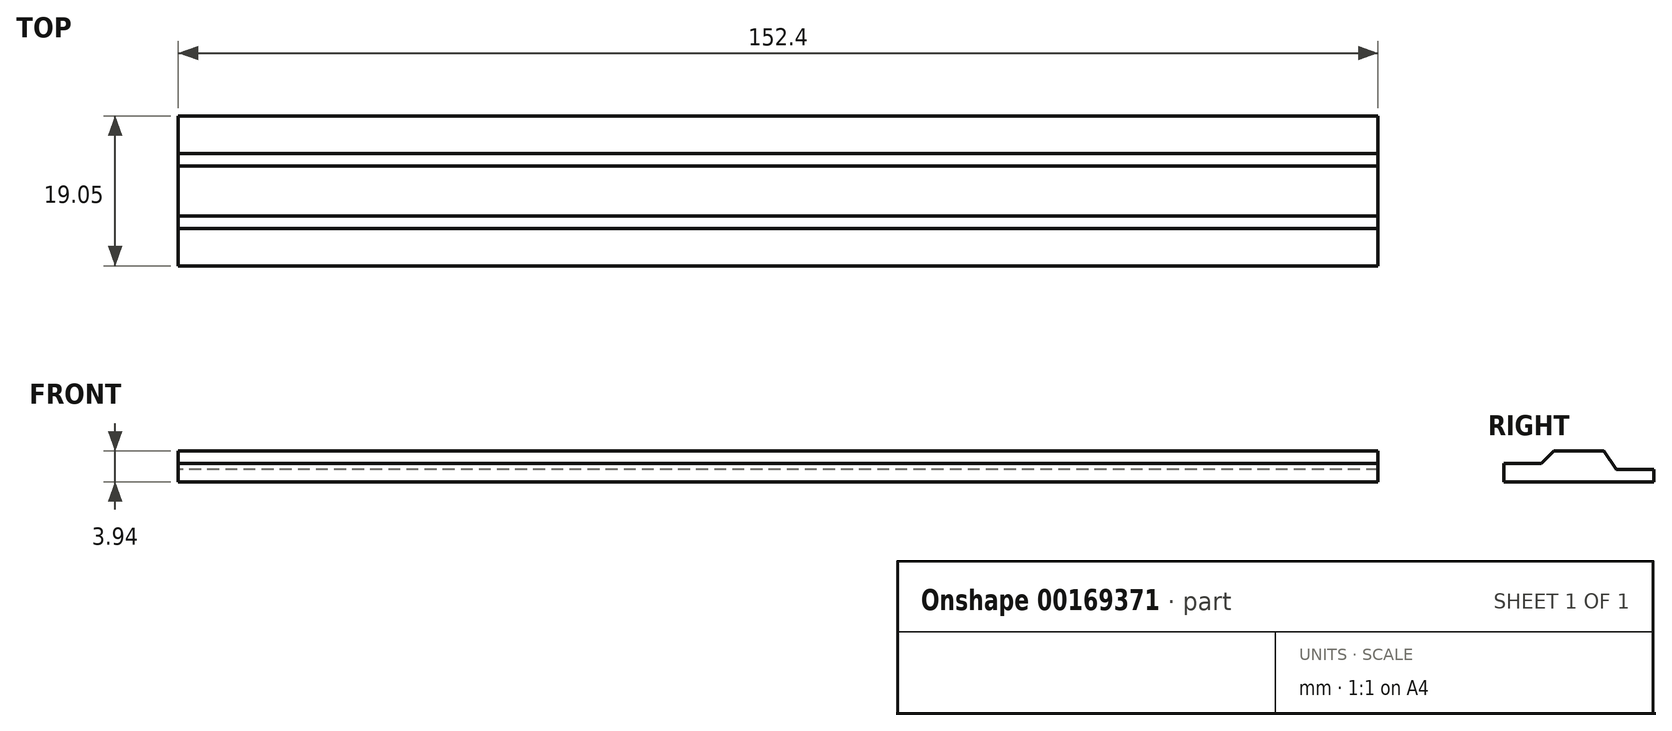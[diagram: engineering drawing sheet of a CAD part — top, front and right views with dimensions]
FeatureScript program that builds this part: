
annotation { "Feature Type Name" : "Feature", "Feature Type Description" : "" }
export const myFeature = defineFeature(function(context is Context, id is Id, definition is map)
    precondition{}
    {
        {
            var Q0;
            Q0=qCreatedBy(makeId("Right.planeOp"),FACE);
            var sketch = newSketch(context, id + "F0", { "sketchPlane" : qUnion([Q0])});
            skLineSegment(sketch, "E0", {"start": v(0, 0) * mm, "end": v(19.05, 0) * mm});
            skLineSegment(sketch, "E1", {"start": v(19.05, 0) * mm, "end": v(19.05, 1.6) * mm});
            skLineSegment(sketch, "E2", {"start": v(19.05, 1.6) * mm, "end": v(14.3, 1.6) * mm});
            skLineSegment(sketch, "E3", {"start": v(0, 0) * mm, "end": v(0, 2.34) * mm});
            skLineSegment(sketch, "E4", {"start": v(0, 2.34) * mm, "end": v(4.75, 2.34) * mm});
            skLineSegment(sketch, "E5", {"start": v(4.75, 2.34) * mm, "end": v(6.35, 3.94) * mm});
            skLineSegment(sketch, "E6", {"start": v(6.35, 3.94) * mm, "end": v(12.7, 3.94) * mm});
            skLineSegment(sketch, "E7", {"start": v(12.7, 3.94) * mm, "end": v(14.3, 1.6) * mm});
            skSolve(sketch);
        }
        {
            var Q0;
            Q0 = qSketchRegion(id + "F0", true);
            extrude(context, id + "F1", {"entities" : qUnion([Q0]), "endBound" : BoundingType.SYMMETRIC, "depth" : 152.4 * mm});
        }
    });
